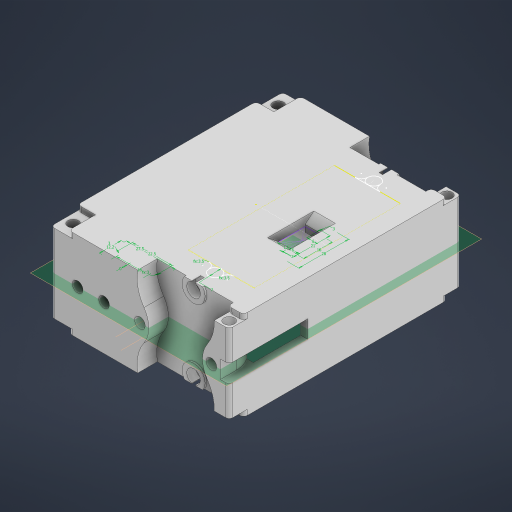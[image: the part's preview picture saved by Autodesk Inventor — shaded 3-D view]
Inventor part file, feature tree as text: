
AUTODESK INVENTOR PART (.ipt)
format: ipt  version: 2024.2 (Build 282272000, 272)  size: 1,561,088 bytes
history: native  units: in
note: dims shown in document units (in); Inventor stores cm internally (conversion verified against a paired STEP export)
features: sketch x45, extrude x41, mirror x16, projected_geometry x12, plane x5, fillet x3, other x2, chamfer x2, revolve x1
ambient origin geometry x8: Origin, YZ Plane, XZ Plane, XY Plane, X Axis, Y Axis, Z Axis, Center Point
bodies: Solid1 (feature_tree)
feature tree (127):
  extrude  "Extrusion1"  Depth=3.937in
  extrude  "Extrusion2"  Depth=0.5906in TaperAngle=0.0deg
  sketch  "Sketch3"  dims[d8=0.2913in d11=0.0472in]
  sketch  "Sketch4"  dims[d12=0.0472in d13=0.253in]
  plane  "Work Plane1"
  mirror  "Mirror1"
  extrude  "Extrusion5"  Depth=0.0472in
  extrude  "Extrusion6"  Depth=0.253in
  extrude  "Extrusion7"  Depth=0.1575in
  sketch  "Sketch9"  dims[d24=0.1339in d25=0.1339in]
  extrude  "Extrusion10"  Depth=1.6535in
  sketch  "Sketch11"  dims[d30=1.3583in d32=0.315in d33=0.0in]
  extrude  "Extrusion11"  Depth=1.1811in
  sketch  "Sketch13"  dims[d34=0.1181in d35=0.1181in]
  other  "Work Axis2"
  revolve  "Revolution1"  [1 undecoded]
  plane  "Work Plane5"
  extrude  "Extrusion13"  Depth=2.1417in
  extrude  "Extrusion14"  Depth=0.315in TaperAngle=0.0deg
  mirror  "Mirror2"
  plane  "Work Plane3"
  extrude  "Extrusion15"  Depth=0.1181in
  plane  "Work Plane4"
  extrude  "Extrusion16"  Depth=0.1181in
  sketch  "Sketch21"  dims[d62=0.1378in d63=0.1378in]
  sketch  "Sketch25"  dims[d66=0.3937in d67=0.1969in]
  extrude  "Extrusion21"  Depth=0.1181in
  extrude  "Extrusion22"  Depth=3.2283in
  mirror  "Mirror4"
  other  "Work Axis3"
  extrude  "Extrusion23"  Depth=1.1811in
  plane  "Work Plane2"
  mirror  "Mirror6"
  extrude  "Extrusion24"  Depth=0.1378in
  mirror  "Mirror7"
  extrude  "Extrusion25"  Depth=0.1969in
  mirror  "Mirror8"
  mirror  "Mirror9"
  mirror  "Mirror10"
  sketch  "Sketch29"  dims[d76=0.7874in d77=0.3937in]
  extrude  "Extrusion28"  Depth=0.1181in TaperAngle=0.0deg
  mirror  "Mirror13"
  mirror  "Mirror14"
  sketch  "Sketch32"  dims[d84=0.3937in d85=0.1969in d86=0.0in]
  extrude  "Extrusion29"  Depth=0.1181in
  extrude  "Extrusion30"  Depth=0.3937in
  mirror  "Mirror15"
  mirror  "Mirror16"
  extrude  "Extrusion31"  Depth=0.3937in
  extrude  "Extrusion32"  Depth=0.7874in
  extrude  "Extrusion33"  Depth=0.1969in TaperAngle=0.0deg
  mirror  "Mirror17"
  mirror  "Mirror18"
  extrude  "Extrusion34"  Depth=0.5906in
  fillet  "Fillet5"  Radius=0.3937in
  fillet  "Fillet6"  Radius=1.378in
  fillet  "Fillet8"  Radius=1.378in
  extrude  "Extrusion36"  Depth=0.7874in
  extrude  "Extrusion37"  Depth=0.2362in
  mirror  "Mirror19"
  mirror  "Mirror20"
  sketch  "Sketch42"  dims[d130=0.3937in d131=0.2953in]
  extrude  "Extrusion42"  Depth=0.2362in
  extrude  "Extrusion43"  Depth=0.7087in
  extrude  "Extrusion45"  Depth=0.5906in
  extrude  "Extrusion46"  Depth=0.3937in
  extrude  "Extrusion47"  Depth=0.1969in
  extrude  "Extrusion48"  Depth=0.1969in TaperAngle=0.0deg
  extrude  "Extrusion49"  Depth=0.3937in
  extrude  "Extrusion50"  Depth=0.1969in TaperAngle=0.0deg
  extrude  "Extrusion51"  Depth=0.2362in
  extrude  "Extrusion52"  Depth=0.7874in
  extrude  "Extrusion53"  Depth=0.2756in
  sketch  "Sketch58"  dims[d171=0.315in d172=0.1181in d173=0.0in]
  extrude  "Extrusion54"  Depth=0.1969in TaperAngle=0.0deg
  extrude  "Extrusion55"  Depth=0.3937in TaperAngle=0.0deg
  extrude  "Extrusion56"  Depth=0.3937in
  extrude  "Extrusion57"  Depth=0.1969in
  extrude  "Extrusion58"  Depth=0.1181in TaperAngle=0.0deg
  chamfer  "Chamfer6"  Distance=0.4331in
  chamfer  "Chamfer7"  Distance=0.5906in
  sketch  "Sketch1"  dims[d0=5.1181in d1=3.937in]
  sketch  "Sketch2"  dims[d2=1.9685in d3=0.0in d4=0.5906in d5=0.0in]
  projected_geometry  "Projected Loop1"
  projected_geometry  "Projected Loop2"
  sketch  "Sketch5"  dims[d14=0.253in d18=0.1575in]
  sketch  "Sketch6"  dims[d19=1.6535in d20=3.7402in]
  sketch  "Sketch7"  dims[d21=1.1811in d22=0.0in d23=0.1339in]
  sketch  "Sketch10"  dims[d26=1.3583in d28=2.1417in]
  projected_geometry  "Projected Loop3"
  projected_geometry  "Projected Loop4"
  sketch  "Sketch16"  dims[d36=0.1181in d37=0.1181in]
  sketch  "Sketch17"  dims[d38=0.1181in d39=0.1181in]
  sketch  "Sketch18"  dims[d49=1.4567in d50=3.2283in]
  sketch  "Sketch19"  dims[d52=1.1811in d53=0.0in d60=0.2756in]
  projected_geometry  "Projected Loop7"
  projected_geometry  "Projected Loop8"
  sketch  "Sketch26"  dims[d68=0.1969in d69=0.1181in d70=0.0in]
  projected_geometry  "Projected Loop10"
  sketch  "Sketch27"  dims[d71=0.1181in d72=0.1181in]
  sketch  "Sketch28"  dims[d73=0.1969in d74=0.0in d75=0.3937in]
  sketch  "Sketch31"  dims[d78=225.0deg d83=0.7874in]
  sketch  "Sketch33"  dims[d87=0.2362in d88=0.5906in d89=0.3937in d90=0.0in d91=1.378in d92=1.378in]
  sketch  "Sketch34"  dims[d93=0.3937in d94=0.0in d95=0.7874in]
  sketch  "Sketch35"  dims[d96=1.1811in d97=0.2362in]
  sketch  "Sketch37"  dims[d99=0.3937in d100=0.0in d101=0.2362in]
  projected_geometry  "Projected Loop11"
  sketch  "Sketch39"  dims[d102=0.1969in d108=0.7087in]
  sketch  "Sketch40"  dims[d110=0.0in d129=0.5906in]
  sketch  "Sketch43"  dims[d132=0.2362in d133=0.1969in]
  sketch  "Sketch44"  dims[d134=0.1181in d135=0.0in d136=0.1969in d137=0.0in]
  sketch  "Sketch46"  dims[d138=0.1969in d139=0.0in d140=0.3937in]
  projected_geometry  "Projected Loop12"
  sketch  "Sketch47"  dims[d141=2.5591in d142=0.1969in d143=0.0in]
  projected_geometry  "Projected Loop13"
  sketch  "Sketch51"  dims[d144=0.1969in d145=0.2362in]
  projected_geometry  "Projected Loop14"
  sketch  "Sketch52"  dims[d146=0.5827in d147=0.7874in]
  projected_geometry  "Projected Loop15"
  sketch  "Sketch53"  dims[d148=0.8268in d149=0.2756in]
  sketch  "Sketch54"  dims[d150=0.1181in d151=0.1969in d152=0.0in]
  sketch  "Sketch55"  dims[d161=1.1811in d162=0.0in d163=0.3937in d164=0.0in]
  sketch  "Sketch56"  dims[d165=0.3937in d166=0.0in d167=0.3937in]
  sketch  "Sketch57"  dims[d168=0.1969in d169=0.0in d170=0.3543in]
  sketch  "Sketch59"  dims[d174=0.2362in]
  sketch  "Sketch60"  dims[d175=0.1575in]
  sketch  "Sketch61"  dims[d176=0.1575in d177=0.4331in d178=0.0in d179=0.5906in d180=0.0787in d182=0.0787in d186=0.1969in d187=0.1969in d188=0.0in d192=0.5512in d193=0.1181in d194=0.0in d200=0.3937in d201=0.0in d202=0.1181in d203=0.8858in d206=0.1181in d207=0.4803in d208=1.0827in d222=1.9685in d223=0.7874in d224=0.0in d225=0.2756in d226=0.0in d227=0.2756in d228=0.0in d231=0.3937in d232=0.3937in d233=0.0in d237=0.0394in d238=0.0787in d239=0.0in d240=0.1575in d241=0.0in d242=0.1575in d243=0.0in d244=0.1575in d245=1.7717in d246=0.0in d247=0.1575in d248=0.1575in d249=0.1969in d250=0.1969in d251=0.1063in d252=0.1181in d253=0.1063in d254=0.1063in d255=0.1063in d256=0.1181in d257=2.3622in d258=0.5512in d259=0.0in d262=0.9843in d263=3.5433in d264=0.0787in d265=1.6929in d266=0.0in d268=0.5906in d269=0.3937in d270=0.3937in d271=0.0in d272=0.7874in d273=0.3937in d274=0.3937in d275=0.0in d276=0.1181in d278=0.8268in d279=0.1181in d280=0.4724in d281=0.2362in d282=0.2362in d283=1.1024in d284=0.6299in d285=0.1181in d286=0.0in d287=0.3937in d288=0.0in d289=0.1969in d290=0.1969in d291=0.3937in d292=0.3937in d293=0.0in d294=0.0787in d295=0.0in d296=0.1181in d297=0.1181in d298=0.0in d299=0.1969in d300=0.1575in d301=45.0deg d302=0.2362in d303=0.2362in d304=45.0deg d305=0.2126in d306=0.2126in d307=0.1181in d308=0.1063in d309=0.1063in d310=1.5748in d311=0.1181in d312=0.0in d313=0.0787in d103=0.0197in d104=0.0344in d105=0.0197in d106=0.0344in d127=0.0in d128=0.0in]
note: 1 required parameter value undecoded (feature->parameter linkage not recoverable at this tier; creation-order binding heuristic only, values carry confidence <= 0.55)
